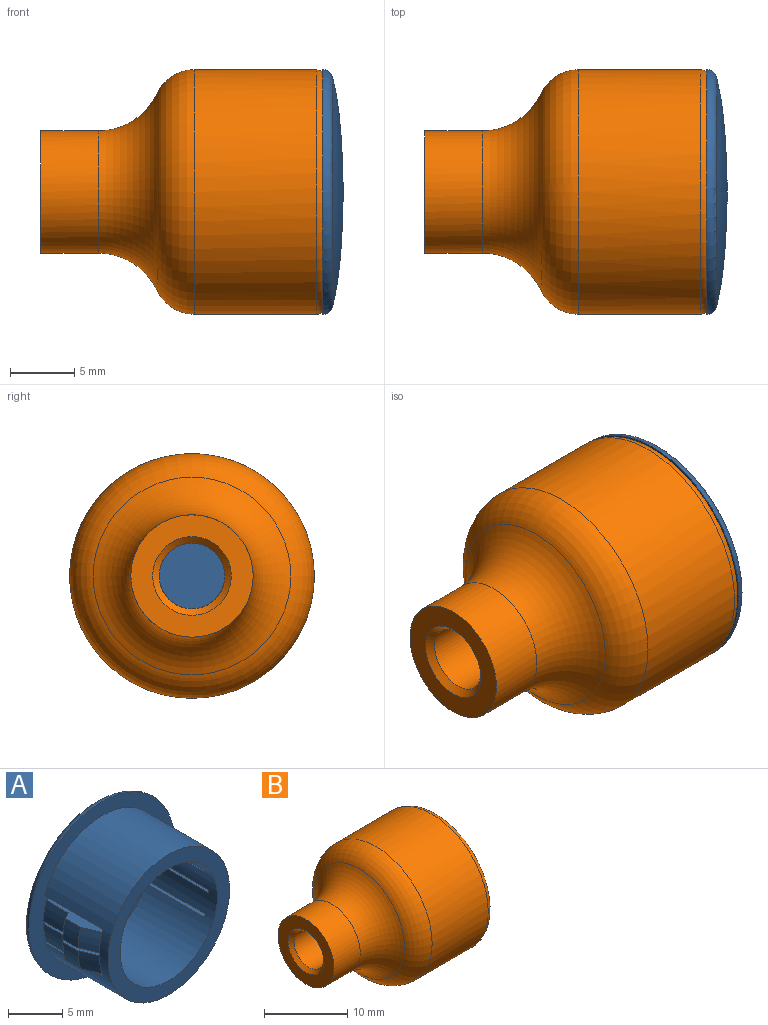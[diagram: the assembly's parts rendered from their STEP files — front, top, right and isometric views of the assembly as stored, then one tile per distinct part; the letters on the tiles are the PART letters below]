
ASSEMBLY  parts=2 mates=1
PART A: 45 faces, bbox 20.6x10.3x20.6 mm
  f0: revolved ~17.9x8.95mm, area 127.2mm2, adj f1,f16
  f1: torus R=8.74mm, axis (0,1,0), area 59.8mm2, adj f0,f16,f18
  f2: cylinder r=6.35mm len=12.7mm, axis (0,1,0), area 330.8mm2, adj f4,f5,f6,f7,f8,f9,f10,f11
  f3: cylinder r=7.94mm len=15.88mm, axis (0,1,0), area 353.8mm2, adj f17,f18,f19,f20,f21,f22,f23,f24
  f4: plane 7.29x2.52mm, normal (0,0,1), area 14.9mm2, adj f2,f14,f19,f37,f38,f39,f40
  f5: plane 7.29x2.52mm, normal (0,0,1), area 14.9mm2, adj f2,f15,f26,f41,f42,f43,f44
  f6: plane 7.28x2.38mm, normal (0,0,1), area 14.1mm2, adj f2,f10,f20,f33,f34,f35,f36
  f7: plane 7.28x2.38mm, normal (0,0,1), area 14.1mm2, adj f2,f11,f25,f29,f30,f31,f32
  f8: plane 7.29x2.52mm, normal (0,0,-1), area 14.9mm2, adj f2,f11,f24,f29,f30,f31,f32
  f9: plane 7.29x2.52mm, normal (0,0,-1), area 14.9mm2, adj f2,f10,f21,f33,f34,f35,f36
  f10: plane 2.18x2.03mm, normal (0,1,0), area 3.5mm2, adj f2,f6,f9,f33
  f11: plane 2.18x2.03mm, normal (0,1,0), area 3.5mm2, adj f2,f7,f8,f30
  f12: plane 7.28x2.38mm, normal (0,0,-1), area 14.1mm2, adj f2,f15,f25,f41,f42,f43,f44
  f13: plane 7.28x2.38mm, normal (0,0,-1), area 14.1mm2, adj f2,f14,f20,f37,f38,f39,f40
  f14: plane 2.18x2.03mm, normal (0,1,0), area 3.5mm2, adj f2,f4,f13,f37
  f15: plane 2.18x2.03mm, normal (0,1,0), area 3.5mm2, adj f2,f5,f12,f43
  f16: revolved ~17.9x8.95mm, area 127.2mm2, adj f0,f1
  f17: plane 15.88x15.88mm, normal (0,-1,0), area 71.3mm2, adj f2,f3
  f18: plane 19.05x19.05mm, normal (0,-1,0), area 231mm2, adj f1,f2,f3,f22,f23,f27,f28
  f19: plane 1.81x0.31mm, normal (0,1,0), area 0.5mm2, adj f2,f3,f4,f23
  f20: plane 1.59x0.31mm, normal (0,1,0), area 0.5mm2, adj f2,f3,f6,f13
  f21: plane 1.81x0.31mm, normal (0,1,0), area 0.5mm2, adj f2,f3,f9,f22
  f22: plane 7.59x1.71mm, normal (0,0,1), area 13mm2, adj f2,f3,f18,f21
  f23: plane 7.59x1.71mm, normal (0,0,-1), area 13mm2, adj f2,f3,f18,f19
  f24: plane 1.81x0.31mm, normal (0,1,0), area 0.5mm2, adj f2,f3,f8,f28
  f25: plane 1.59x0.31mm, normal (0,1,0), area 0.5mm2, adj f2,f3,f7,f12
  f26: plane 1.81x0.31mm, normal (0,1,0), area 0.5mm2, adj f2,f3,f5,f27
  f27: plane 7.59x1.71mm, normal (0,0,-1), area 13mm2, adj f2,f3,f18,f26
  f28: plane 7.59x1.71mm, normal (0,0,1), area 13mm2, adj f2,f3,f18,f24
  f29: cylinder r=8.73mm len=2.18mm, axis (0,1,0), area 4.4mm2, adj f7,f8,f31,f32
  f30: cylinder r=7.94mm len=2.86mm, axis (0,1,0), area 6.3mm2, adj f7,f8,f11,f31
  f31: cone r=7.94mm half-angle=60deg, axis (0,-1,0), area 2mm2, adj f7,f8,f29,f30
  f32: cone r=8.73mm half-angle=21.8deg, axis (0,1,0), area 4.7mm2, adj f3,f7,f8,f29
  f33: cylinder r=7.94mm len=2.86mm, axis (0,1,0), area 6.3mm2, adj f6,f9,f10,f35
  f34: cylinder r=8.73mm len=2.18mm, axis (0,1,0), area 4.4mm2, adj f6,f9,f35,f36
  f35: cone r=7.94mm half-angle=60deg, axis (0,-1,0), area 2mm2, adj f6,f9,f33,f34
  f36: cone r=8.73mm half-angle=21.8deg, axis (0,1,0), area 4.7mm2, adj f3,f6,f9,f34
  f37: cylinder r=7.94mm len=2.86mm, axis (0,1,0), area 6.3mm2, adj f4,f13,f14,f39
  f38: cylinder r=8.73mm len=2.18mm, axis (0,1,0), area 4.4mm2, adj f4,f13,f39,f40
  f39: cone r=7.94mm half-angle=60deg, axis (0,-1,0), area 2mm2, adj f4,f13,f37,f38
  f40: cone r=8.73mm half-angle=21.8deg, axis (0,1,0), area 4.7mm2, adj f3,f4,f13,f38
  f41: cylinder r=8.73mm len=2.18mm, axis (0,1,0), area 4.4mm2, adj f5,f12,f42,f44
  f42: cone r=8.73mm half-angle=21.8deg, axis (0,1,0), area 4.7mm2, adj f3,f5,f12,f41
  f43: cylinder r=7.94mm len=2.86mm, axis (0,1,0), area 6.3mm2, adj f5,f12,f15,f44
  f44: cone r=7.94mm half-angle=60deg, axis (0,-1,0), area 2mm2, adj f5,f12,f41,f43
PART B: 13 faces, bbox 22.2x21.3x21.3 mm
  f0: cylinder r=9.53mm len=19.05mm, axis (1,0,0), area 570.2mm2, adj f5,f9
  f1: plane 17.53x17.53mm, normal (1,0,0), area 44.6mm2, adj f6,f9
  f2: cylinder r=4.76mm len=9.53mm, axis (1,0,0), area 133.3mm2, adj f3,f4
  f3: plane 9.53x9.53mm, normal (-1,0,0), area 41.8mm2, adj f2,f11
  f4: torus R=9.84mm, axis (1,0,0), area 209.3mm2, adj f2,f5
  f5: torus R=6.35mm, axis (-1,0,0), area 201mm2, adj f0,f4
  f6: cylinder r=7.91mm len=15.82mm, axis (1,0,0), area 460.9mm2, adj f1,f12
  f7: plane 14.05x14.05mm, normal (1,0,0), area 125.5mm2, adj f10,f12
  f8: cylinder r=2.55mm len=11.05mm, axis (1,0,0), area 177.2mm2, adj f10,f11
  f9: torus R=8.76mm, axis (1,0,0), area 69.6mm2, adj f0,f1
  f10: cone r=2.55mm half-angle=45deg, axis (1,0,0), area 12.7mm2, adj f7,f8
  f11: cone r=3.06mm half-angle=45deg, axis (-1,0,0), area 12.7mm2, adj f3,f8
  f12: torus R=7.02mm, axis (1,0,0), area 66.6mm2, adj f6,f7
PLACE A rot(axis=(0.58,0.58,-0.58),120deg) t=(-3.1,-5.55,5.13)mm
PLACE B t=(-2.83,-5.55,5.13)mm
MATE cylindrical A.f1 <-> B.f0  axis (1,0,0) through (-7.46,-5.55,5.13)mm
